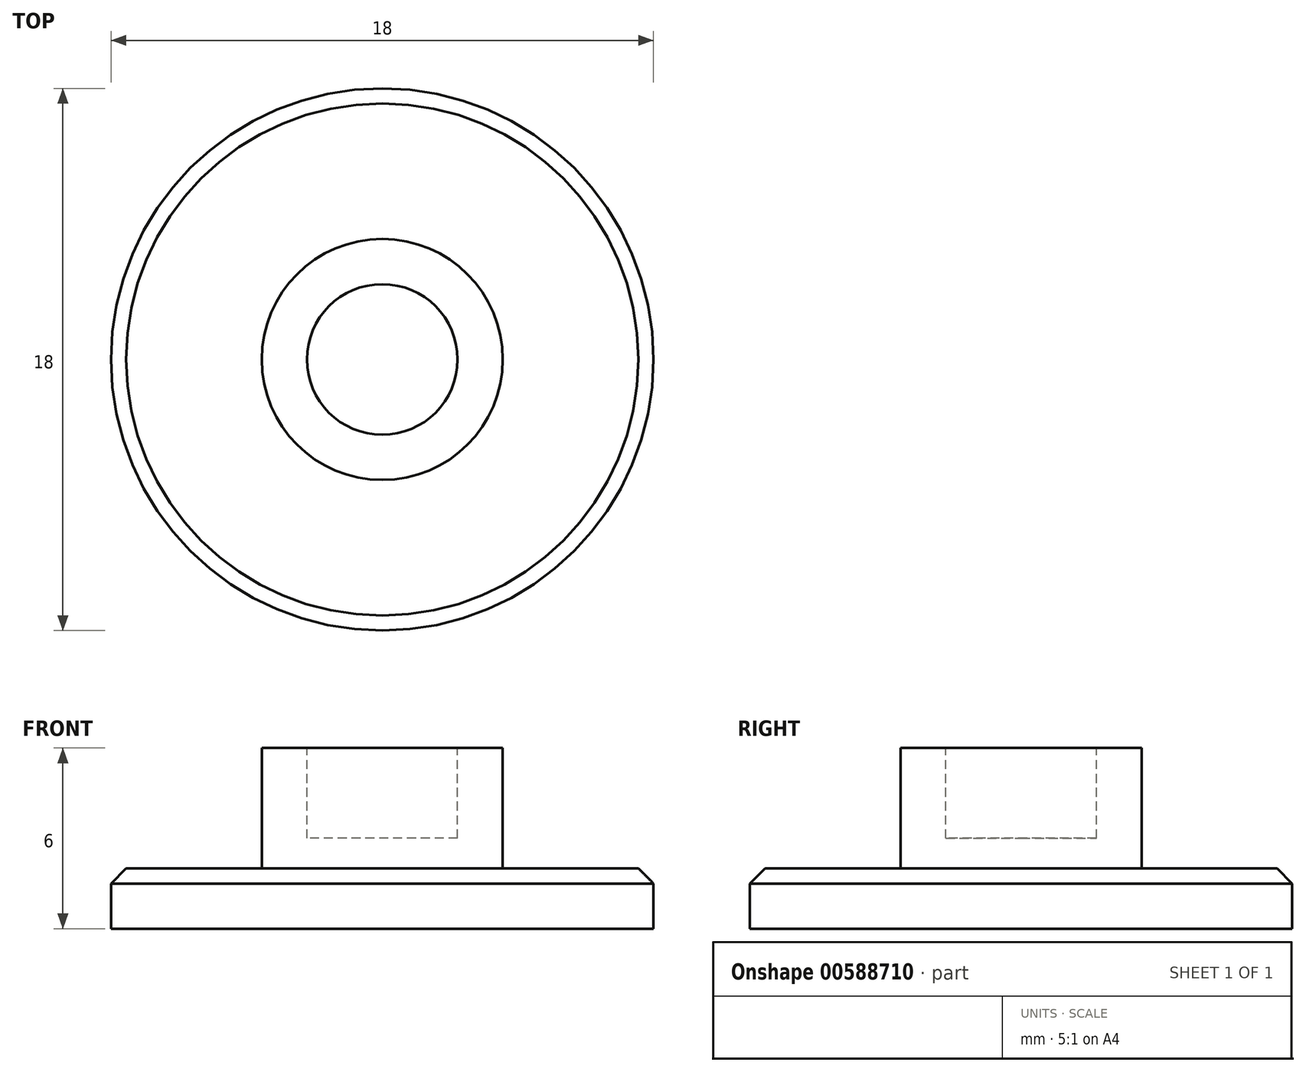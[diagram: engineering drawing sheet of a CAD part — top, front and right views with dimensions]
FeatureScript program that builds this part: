
annotation { "Feature Type Name" : "Feature", "Feature Type Description" : "" }
export const myFeature = defineFeature(function(context is Context, id is Id, definition is map)
    precondition{}
    {
        {
            var Q0;
            Q0=qCreatedBy(makeId("Top.planeOp"),FACE);
            var sketch = newSketch(context, id + "F0", { "sketchPlane" : qUnion([Q0])});
            skCircle(sketch, "E0", {"center": v(0, 0) * mm, "radius": 9 * mm});
            skSolve(sketch);
        }
        {
            var Q0;
            Q0 = qSketchRegion(id + "F0", true);
            extrude(context, id + "F1", {"entities" : qUnion([Q0]), "depth" : 2 * mm, "offsetDistance" : 25 * mm});
        }
        {
            var Q0;
            Q0=makeQuery(id+"F1.opExtrude","CAP_FACE",FACE,{"disambiguationData":[OSD([sQuery(id+"F0.wireOp",EDGE,"E0")])],"isStart":false});
            var sketch = newSketch(context, id + "F2", { "sketchPlane" : qUnion([Q0])});
            skCircle(sketch, "E1", {"center": v(0, 0) * mm, "radius": 4 * mm});
            skSolve(sketch);
        }
        {
            var Q0;
            Q0 = qSketchRegion(id + "F2", true);
            extrude(context, id + "F3", {"entities" : qUnion([Q0]), "operationType" : NewBodyOperationType.ADD, "depth" : 4 * mm, "offsetDistance" : 25 * mm});
        }
        {
            var Q0;
            Q0=makeQuery(id+"F3.opExtrude","CAP_FACE",FACE,{"disambiguationData":[OSD([sQuery(id+"F2.wireOp",EDGE,"E1")])],"isStart":false});
            var sketch = newSketch(context, id + "F4", { "sketchPlane" : qUnion([Q0])});
            skCircle(sketch, "E2", {"center": v(0, 0) * mm, "radius": 2.5 * mm});
            skSolve(sketch);
        }
        {
            var Q0;
            Q0 = qSketchRegion(id + "F4", true);
            extrude(context, id + "F5", {"entities" : qUnion([Q0]), "operationType" : NewBodyOperationType.REMOVE, "oppositeDirection" : true, "depth" : 3 * mm, "offsetDistance" : 25 * mm});
        }
        {
            var Q0;
            Q0=makeQuery(id+"F1.opExtrude","CAP_EDGE",EDGE,{"disambiguationData":[OSD([sQuery(id+"F0.wireOp",EDGE,"E0")])],"isStart":false});
            chamfer(context, id + "F6", {"entities" : qUnion([Q0]), "width" : .5 * mm, "tangentPropagation" : true});
        }
    });
